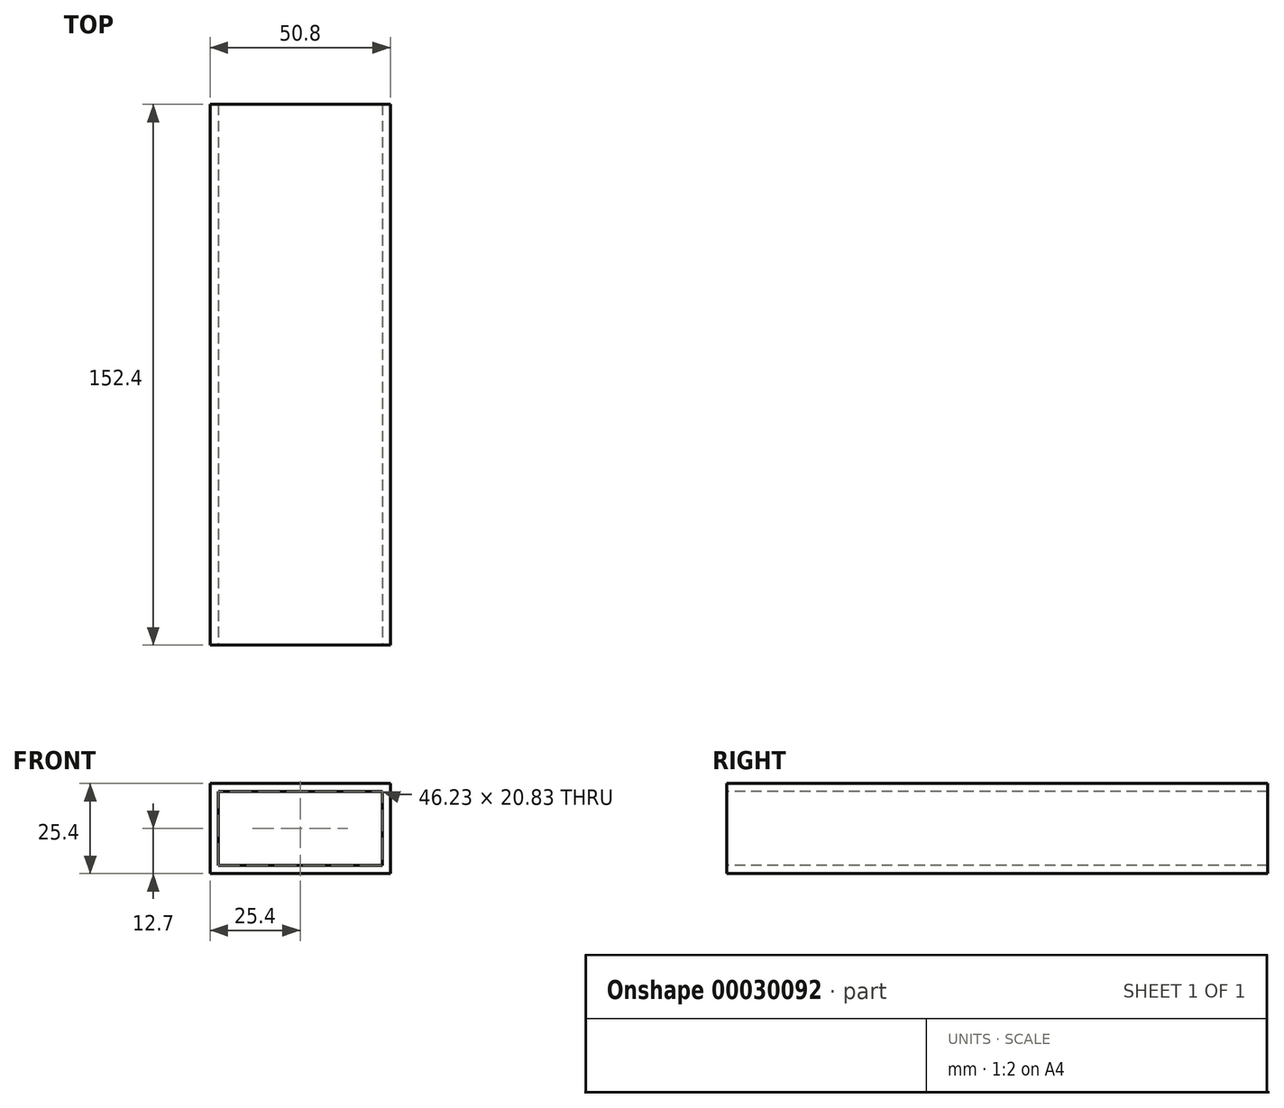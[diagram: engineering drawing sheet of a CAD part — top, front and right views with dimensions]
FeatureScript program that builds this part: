
annotation { "Feature Type Name" : "Feature", "Feature Type Description" : "" }
export const myFeature = defineFeature(function(context is Context, id is Id, definition is map)
    precondition{}
    {
        {
            var Q0;
            Q0=qCreatedBy(makeId("Front.planeOp"),FACE);
            var sketch = newSketch(context, id + "F0", { "sketchPlane" : qUnion([Q0])});
            skLineSegment(sketch, "E0.bottom", {"start": v(0, 0) * mm, "end": v(50.8, 0) * mm});
            skLineSegment(sketch, "E0.top", {"start": v(0, 25.4) * mm, "end": v(50.8, 25.4) * mm});
            skLineSegment(sketch, "E0.left", {"start": v(0, 0) * mm, "end": v(0, 25.4) * mm});
            skLineSegment(sketch, "E0.right", {"start": v(50.8, 0) * mm, "end": v(50.8, 25.4) * mm});
            skSolve(sketch);
        }
        {
            var Q0;
            Q0 = qSketchRegion(id + "F0", true);
            extrude(context, id + "F1", {"entities" : qUnion([Q0]), "oppositeDirection" : true, "depth" : 152.4 * mm});
        }
        {
            var Q0;
            Q0=makeQuery(id+"F1.opExtrude","CAP_FACE",FACE,{"disambiguationData":[OSD([sQuery(id+"F0.wireOp",EDGE,"E0.bottom"),sQuery(id+"F0.wireOp",EDGE,"E0.top"),sQuery(id+"F0.wireOp",EDGE,"E0.left"),sQuery(id+"F0.wireOp",EDGE,"E0.right")])],"isStart":true});
            var sketch = newSketch(context, id + "F2", { "sketchPlane" : qUnion([Q0])});
            skLineSegment(sketch, "E1.0", {"start": v(2.29, 23.11) * mm, "end": v(2.29, 2.29) * mm});
            skLineSegment(sketch, "E1.1", {"start": v(48.51, 23.11) * mm, "end": v(2.29, 23.11) * mm});
            skLineSegment(sketch, "E1.2", {"start": v(48.51, 2.29) * mm, "end": v(48.51, 23.11) * mm});
            skLineSegment(sketch, "E1.3", {"start": v(2.29, 2.29) * mm, "end": v(48.51, 2.29) * mm});
            skSolve(sketch);
        }
        {
            var Q0;
            Q0 = qSketchRegion(id + "F2", true);
            extrude(context, id + "F3", {"entities" : qUnion([Q0]), "operationType" : NewBodyOperationType.REMOVE, "endBound" : BoundingType.THROUGH_ALL, "oppositeDirection" : true, "depth" : 25.4 * mm});
        }
    });
